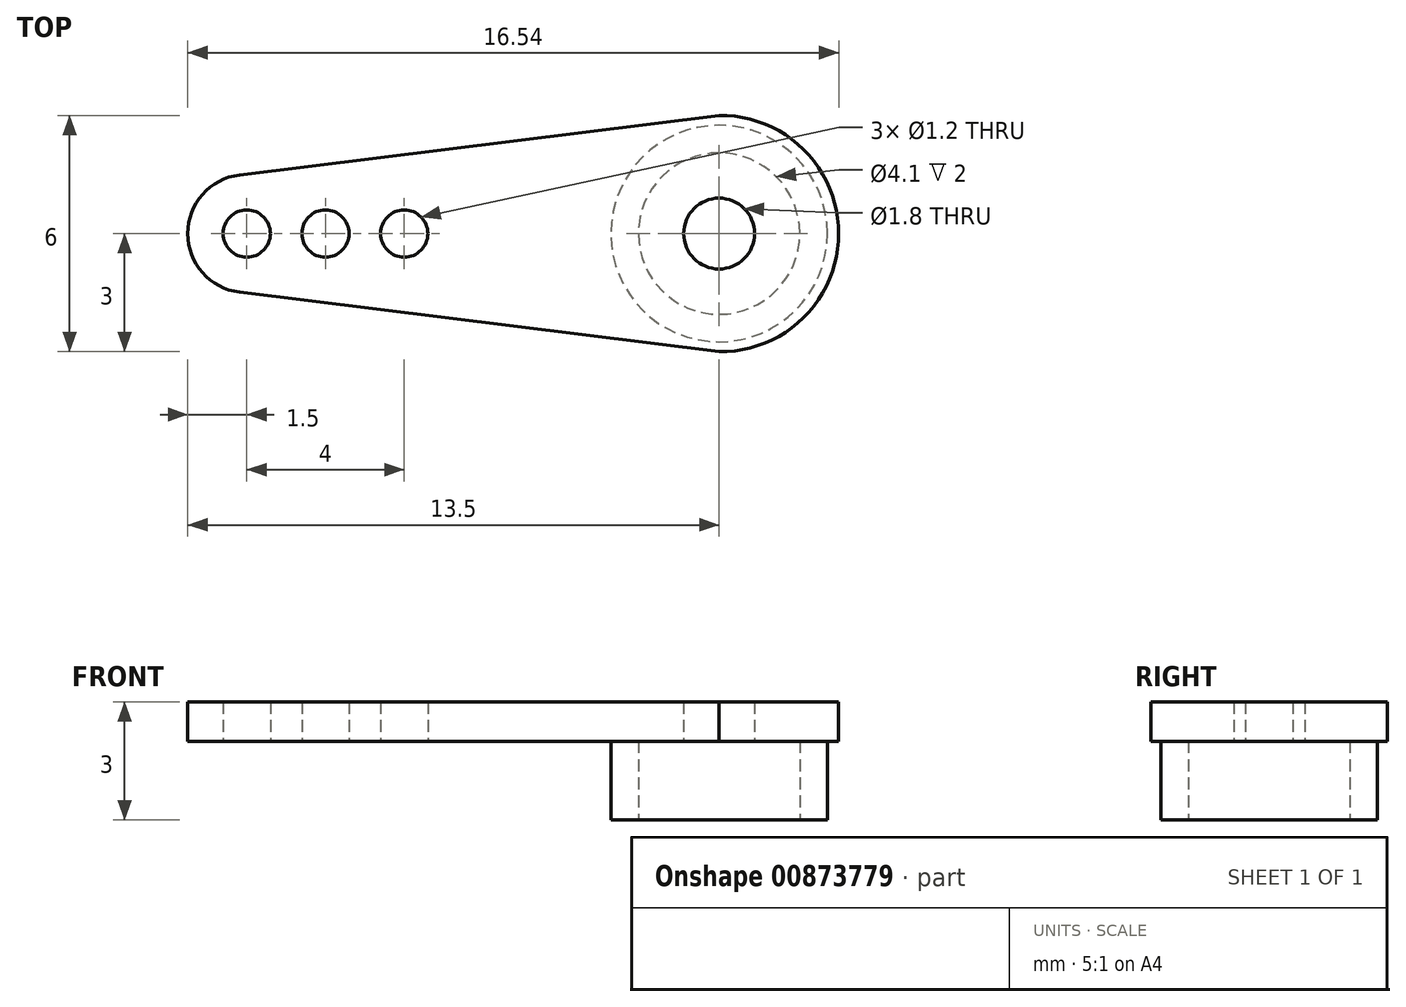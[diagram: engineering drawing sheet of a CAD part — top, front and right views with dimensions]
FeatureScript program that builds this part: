
annotation { "Feature Type Name" : "Feature", "Feature Type Description" : "" }
export const myFeature = defineFeature(function(context is Context, id is Id, definition is map)
    precondition{}
    {
        {
            var Q0;
            Q0=qCreatedBy(makeId("Top.planeOp"),FACE);
            var sketch = newSketch(context, id + "F0", { "sketchPlane" : qUnion([Q0])});
            skCircle(sketch, "E0", {"center": v(0, 0) * mm, "radius": 2.75 * mm});
            skCircle(sketch, "E1", {"center": v(0, 0) * mm, "radius": 2.05 * mm});
            skSolve(sketch);
        }
        {
            var Q0;
            Q0 = qSketchRegion(id + "F0", true);
            extrude(context, id + "F1", {"entities" : qUnion([Q0]), "depth" : 2 * mm, "offsetDistance" : 25 * mm});
        }
        {
            var Q0;
            Q0=makeQuery(id+"F1.opExtrude","CAP_FACE",FACE,{"disambiguationData":[OSD([sQuery(id+"F0.wireOp",EDGE,"E0"),sQuery(id+"F0.wireOp",EDGE,"E1")])],"isStart":false});
            var sketch = newSketch(context, id + "F2", { "sketchPlane" : qUnion([Q0])});
            skPoint(sketch, "E2.middle", {"position": v(0, 0) * mm});
            skCircle(sketch, "E3", {"center": v(-12, 0) * mm, "radius": 1.5 * mm});
            skLineSegment(sketch, "E4", {"start": v(0, 3) * mm, "end": v(-12.18, 1.49) * mm});
            skLineSegment(sketch, "E5", {"start": v(0, -3) * mm, "end": v(-12.18, -1.49) * mm});
            skCircle(sketch, "E6", {"center": v(0, 0) * mm, "radius": 0.9 * mm});
            skCircle(sketch, "E7", {"center": v(-12, 0) * mm, "radius": 0.6 * mm});
            skCircle(sketch, "E8", {"center": v(-10, 0) * mm, "radius": 0.6 * mm});
            skCircle(sketch, "E9", {"center": v(-8, 0) * mm, "radius": 0.6 * mm});
            skArc(sketch, "E10", {"start": v(0, -3) * mm, "mid": v(3.04, 0) * mm, "end": v(0, 3) * mm});
            skSolve(sketch);
        }
        {
            var Q0;
            Q0 = qSketchRegion(id + "F2", true);
            extrude(context, id + "F3", {"entities" : qUnion([Q0]), "operationType" : NewBodyOperationType.ADD, "depth" : 1 * mm, "offsetDistance" : 25 * mm});
        }
    });
